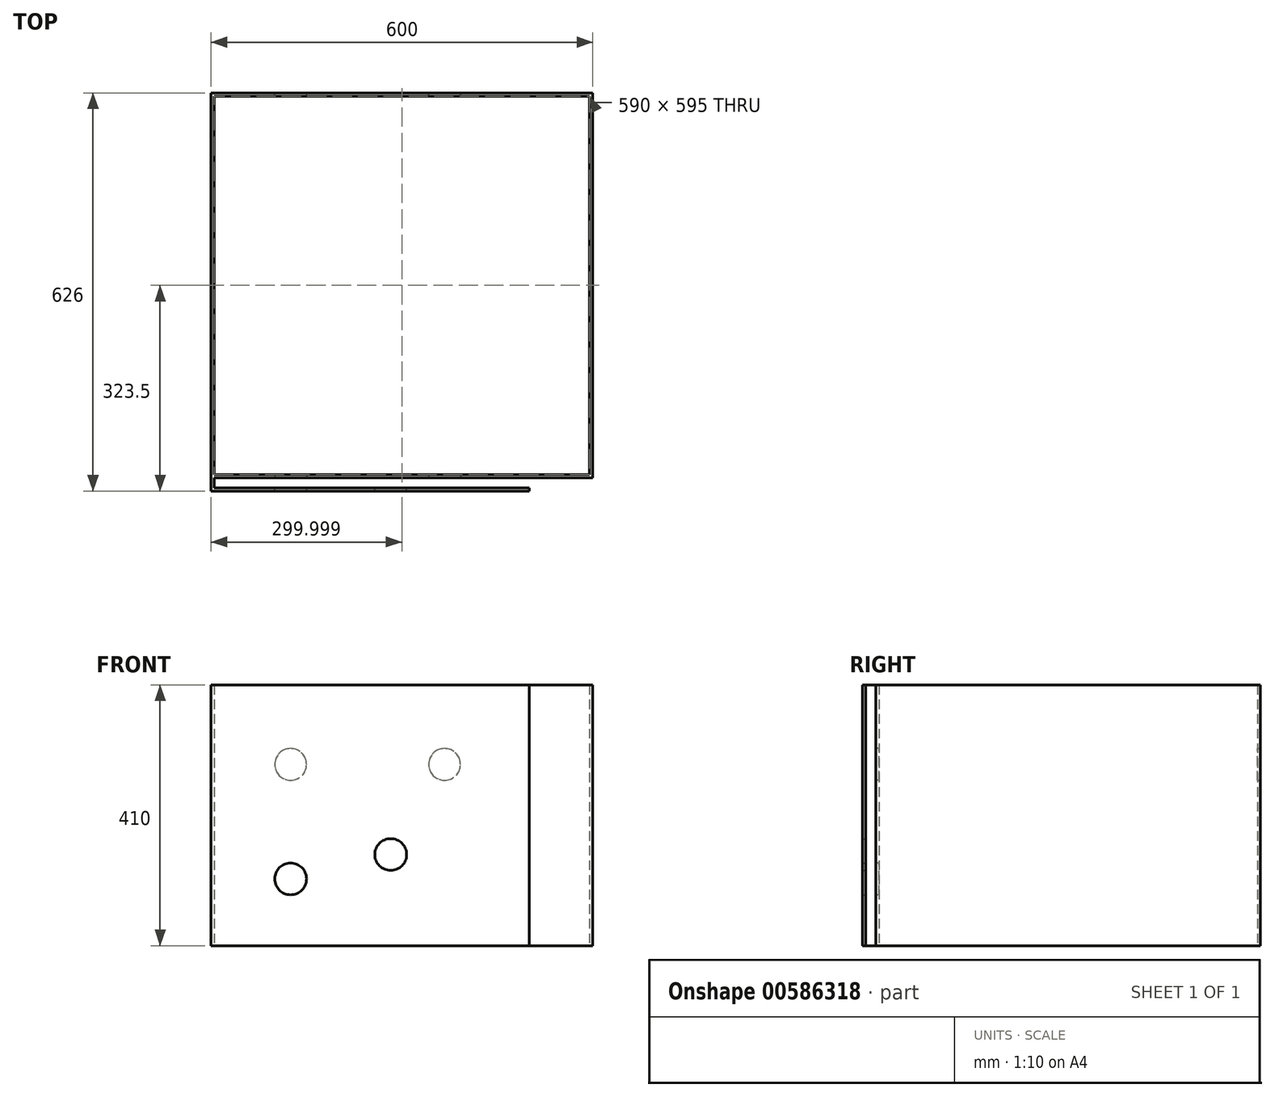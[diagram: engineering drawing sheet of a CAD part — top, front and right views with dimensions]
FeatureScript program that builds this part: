
annotation { "Feature Type Name" : "Feature", "Feature Type Description" : "" }
export const myFeature = defineFeature(function(context is Context, id is Id, definition is map)
    precondition{}
    {
        {
            var Q0;
            Q0=qCreatedBy(makeId("Front.planeOp"),FACE);
            var sketch = newSketch(context, id + "F0", { "sketchPlane" : qUnion([Q0])});
            skLineSegment(sketch, "E0.bottom", {"start": v(-123.13, -99.56) * mm, "end": v(476.87, -99.56) * mm});
            skLineSegment(sketch, "E0.top", {"start": v(-123.13, 310.44) * mm, "end": v(476.87, 310.44) * mm});
            skLineSegment(sketch, "E0.left", {"start": v(-123.13, -99.56) * mm, "end": v(-123.13, 310.44) * mm});
            skLineSegment(sketch, "E0.right", {"start": v(476.87, -99.56) * mm, "end": v(476.87, 310.44) * mm});
            skSolve(sketch);
        }
        {
            var Q0;
            Q0=qSketchRegion(id+"F0",true);
            extrude(context, id + "F1", {"entities" : qUnion([Q0]), "depth" : 5 * mm, "offsetDistance" : 25.4 * mm});
        }
        {
            var Q0;
            Q0=makeQuery(id+"F1.opExtrude","CAP_FACE",FACE,{"disambiguationData":[OSD([sQuery(id+"F0.wireOp",EDGE,"E0.bottom"),sQuery(id+"F0.wireOp",EDGE,"E0.top"),sQuery(id+"F0.wireOp",EDGE,"E0.left"),sQuery(id+"F0.wireOp",EDGE,"E0.right")])],"isStart":false});
            var sketch = newSketch(context, id + "F2", { "sketchPlane" : qUnion([Q0])});
            skPoint(sketch, "E1", {"position": v(1.87, 185.44) * mm});
            skPoint(sketch, "E2", {"position": v(1.87, 5.44) * mm});
            skPoint(sketch, "E3", {"position": v(243.87, 185.44) * mm});
            skPoint(sketch, "E4", {"position": v(159.27, 43.78) * mm});
            skCircle(sketch, "E5", {"center": v(1.87, 185.44) * mm, "radius": 25 * mm});
            skCircle(sketch, "E6", {"center": v(243.87, 185.44) * mm, "radius": 25 * mm});
            skCircle(sketch, "E7", {"center": v(1.87, 5.44) * mm, "radius": 25 * mm});
            skCircle(sketch, "E8", {"center": v(159.27, 43.78) * mm, "radius": 25 * mm});
            skLineSegment(sketch, "E9.bottom", {"start": v(-123.13, 310.44) * mm, "end": v(-118.13, 310.44) * mm});
            skLineSegment(sketch, "E9.top", {"start": v(-123.13, -99.56) * mm, "end": v(-118.13, -99.56) * mm});
            skLineSegment(sketch, "E9.left", {"start": v(-123.13, 310.44) * mm, "end": v(-123.13, -99.56) * mm});
            skLineSegment(sketch, "E9.right", {"start": v(-118.13, 310.44) * mm, "end": v(-118.13, -99.56) * mm});
            skSolve(sketch);
        }
        {
            var Q0;
            Q0=makeQuery(id+"F1.opExtrude","CAP_FACE",FACE,{"disambiguationData":[OSD([sQuery(id+"F0.wireOp",EDGE,"E0.bottom"),sQuery(id+"F0.wireOp",EDGE,"E0.top"),sQuery(id+"F0.wireOp",EDGE,"E0.left"),sQuery(id+"F0.wireOp",EDGE,"E0.right")])],"isStart":true});
            var sketch = newSketch(context, id + "F3", { "sketchPlane" : qUnion([Q0])});
            skLineSegment(sketch, "E10.bottom", {"start": v(-476.87, 310.44) * mm, "end": v(-471.87, 310.44) * mm});
            skLineSegment(sketch, "E10.top", {"start": v(-476.87, -99.56) * mm, "end": v(-471.87, -99.56) * mm});
            skLineSegment(sketch, "E10.left", {"start": v(-476.87, 310.44) * mm, "end": v(-476.87, -99.56) * mm});
            skLineSegment(sketch, "E10.right", {"start": v(-471.87, 310.44) * mm, "end": v(-471.87, -99.56) * mm});
            skLineSegment(sketch, "E11.bottom", {"start": v(123.13, 310.44) * mm, "end": v(118.13, 310.44) * mm});
            skLineSegment(sketch, "E11.top", {"start": v(123.13, -99.56) * mm, "end": v(118.13, -99.56) * mm});
            skLineSegment(sketch, "E11.left", {"start": v(123.13, 310.44) * mm, "end": v(123.13, -99.56) * mm});
            skLineSegment(sketch, "E11.right", {"start": v(118.13, 310.44) * mm, "end": v(118.13, -99.56) * mm});
            skSolve(sketch);
        }
        {
            var Q0;
            Q0=qSketchRegion(id+"F3",true);
            extrude(context, id + "F4", {"entities" : qUnion([Q0]), "operationType" : NewBodyOperationType.ADD, "depth" : 600 * mm, "offsetDistance" : 25.4 * mm});
        }
        {
            var Q0;
            Q0=makeQuery(id+"F4.opExtrude","SWEPT_FACE",FACE,{"disambiguationData":[OSD([sQuery(id+"F3.wireOp",EDGE,"E10.right")])]});
            var sketch = newSketch(context, id + "F5", { "sketchPlane" : qUnion([Q0])});
            skLineSegment(sketch, "E12.bottom", {"start": v(-600, 310.44) * mm, "end": v(-595, 310.44) * mm});
            skLineSegment(sketch, "E12.top", {"start": v(-600, -99.56) * mm, "end": v(-595, -99.56) * mm});
            skLineSegment(sketch, "E12.left", {"start": v(-600, 310.44) * mm, "end": v(-600, -99.56) * mm});
            skLineSegment(sketch, "E12.right", {"start": v(-595, 310.44) * mm, "end": v(-595, -99.56) * mm});
            skSolve(sketch);
        }
        {
            var Q0;
            Q0=qSketchRegion(id+"F5",true);
            extrude(context, id + "F6", {"entities" : qUnion([Q0]), "operationType" : NewBodyOperationType.ADD, "depth" : 591 * mm, "offsetDistance" : 25.4 * mm});
        }
        {
            var Q0;
            Q0=makeQuery(id+"F6.boolean.opBoolean","MERGE",FACE,{"derivedFrom":[makeQuery(id+"F4.opExtrude","CAP_FACE",FACE,{"disambiguationData":[OSD([sQuery(id+"F3.wireOp",EDGE,"E10.bottom"),sQuery(id+"F3.wireOp",EDGE,"E10.top"),sQuery(id+"F3.wireOp",EDGE,"E10.left"),sQuery(id+"F3.wireOp",EDGE,"E10.right")])],"isStart":false}),makeQuery(id+"F4.opExtrude","CAP_FACE",FACE,{"disambiguationData":[OSD([sQuery(id+"F3.wireOp",EDGE,"E11.bottom"),sQuery(id+"F3.wireOp",EDGE,"E11.top"),sQuery(id+"F3.wireOp",EDGE,"E11.left"),sQuery(id+"F3.wireOp",EDGE,"E11.right")])],"isStart":false}),makeQuery(id+"F6.opExtrude","SWEPT_FACE",FACE,{"disambiguationData":[OSD([sQuery(id+"F5.wireOp",EDGE,"E12.left")])]})]});
            var sketch = newSketch(context, id + "F7", { "sketchPlane" : qUnion([Q0])});
            skPoint(sketch, "E13", {"position": v(-1.87, 185.44) * mm});
            skCircle(sketch, "E14", {"center": v(-1.87, 185.44) * mm, "radius": 25 * mm});
            skPoint(sketch, "E15", {"position": v(-243.87, 185.44) * mm});
            skCircle(sketch, "E16", {"center": v(-243.87, 185.44) * mm, "radius": 25 * mm});
            skSolve(sketch);
        }
        {
            var Q0;
            Q0=qSketchRegion(id+"F7",true);
            extrude(context, id + "F8", {"entities" : qUnion([Q0]), "operationType" : NewBodyOperationType.REMOVE, "oppositeDirection" : true, "depth" : 25.4 * mm, "offsetDistance" : 25.4 * mm});
        }
        {
            var Q0;
            Q0=makeQuery(id+"F2.imprint","IMPRINT",FACE,{"disambiguationData":[TD([[makeQuery(id+"F2.imprint","IMPRINT",EDGE,{"derivedFrom":sQuery(id+"F2.wireOp",EDGE,"E5")}),1.0]])]});
            extrude(context, id + "F9", {"entities" : qUnion([Q0]), "operationType" : NewBodyOperationType.REMOVE, "oppositeDirection" : true, "depth" : 25.4 * mm, "offsetDistance" : 25.4 * mm});
        }
        {
            var Q0;
            Q0=makeQuery(id+"F2.imprint","IMPRINT",FACE,{"disambiguationData":[TD([[makeQuery(id+"F2.imprint","IMPRINT",EDGE,{"derivedFrom":sQuery(id+"F2.wireOp",EDGE,"E6")}),1.0]])]});
            extrude(context, id + "F10", {"entities" : qUnion([Q0]), "operationType" : NewBodyOperationType.REMOVE, "oppositeDirection" : true, "depth" : 25.4 * mm, "offsetDistance" : 25.4 * mm});
        }
        {
            var Q0;
            Q0=makeQuery(id+"F2.imprint","IMPRINT",FACE,{"disambiguationData":[TD([[makeQuery(id+"F2.imprint","IMPRINT",EDGE,{"derivedFrom":sQuery(id+"F2.wireOp",EDGE,"E7")}),1.0]])]});
            extrude(context, id + "F11", {"entities" : qUnion([Q0]), "operationType" : NewBodyOperationType.REMOVE, "oppositeDirection" : true, "depth" : 25.4 * mm, "offsetDistance" : 25.4 * mm});
        }
        {
            var Q0;
            Q0=makeQuery(id+"F2.imprint","IMPRINT",FACE,{"disambiguationData":[TD([[makeQuery(id+"F2.imprint","IMPRINT",EDGE,{"derivedFrom":sQuery(id+"F2.wireOp",EDGE,"E9.bottom")}),-1.0]])]});
            extrude(context, id + "F12", {"entities" : qUnion([Q0]), "operationType" : NewBodyOperationType.ADD, "depth" : 21 * mm, "offsetDistance" : 25.4 * mm});
        }
        {
            var Q0;
            Q0=makeQuery(id+"F12.opExtrude","SWEPT_FACE",FACE,{"disambiguationData":[OSD([sQuery(id+"F2.wireOp",EDGE,"E9.right")])]});
            var sketch = newSketch(context, id + "F13", { "sketchPlane" : qUnion([Q0])});
            skLineSegment(sketch, "E17.bottom", {"start": v(-26, 310.44) * mm, "end": v(-21, 310.44) * mm});
            skLineSegment(sketch, "E17.top", {"start": v(-26, -99.56) * mm, "end": v(-21, -99.56) * mm});
            skLineSegment(sketch, "E17.left", {"start": v(-26, 310.44) * mm, "end": v(-26, -99.56) * mm});
            skLineSegment(sketch, "E17.right", {"start": v(-21, 310.44) * mm, "end": v(-21, -99.56) * mm});
            skSolve(sketch);
        }
        {
            var Q0;
            Q0=qSketchRegion(id+"F13",true);
            extrude(context, id + "F14", {"entities" : qUnion([Q0]), "operationType" : NewBodyOperationType.ADD, "depth" : 495 * mm, "offsetDistance" : 25.4 * mm});
        }
        {
            var Q0;
            Q0=makeQuery(id+"F2.imprint","IMPRINT",FACE,{"disambiguationData":[TD([[makeQuery(id+"F2.imprint","IMPRINT",EDGE,{"derivedFrom":sQuery(id+"F2.wireOp",EDGE,"E7")}),1.0]])]});
            extrude(context, id + "F15", {"entities" : qUnion([Q0]), "operationType" : NewBodyOperationType.REMOVE, "depth" : 76.2 * mm, "offsetDistance" : 25.4 * mm});
        }
        {
            var Q0;
            Q0=makeQuery(id+"F2.imprint","IMPRINT",FACE,{"disambiguationData":[TD([[makeQuery(id+"F2.imprint","IMPRINT",EDGE,{"derivedFrom":sQuery(id+"F2.wireOp",EDGE,"E8")}),1.0]])]});
            var Q1;
            Q1=sQuery(id+"F2.wireOp",EDGE,"E8");
            extrude(context, id + "F16", {"entities" : qUnion([Q0]), "operationType" : NewBodyOperationType.REMOVE, "surfaceEntities" : qUnion([Q1]), "depth" : 25.4 * mm, "offsetDistance" : 25.4 * mm});
        }
    });
